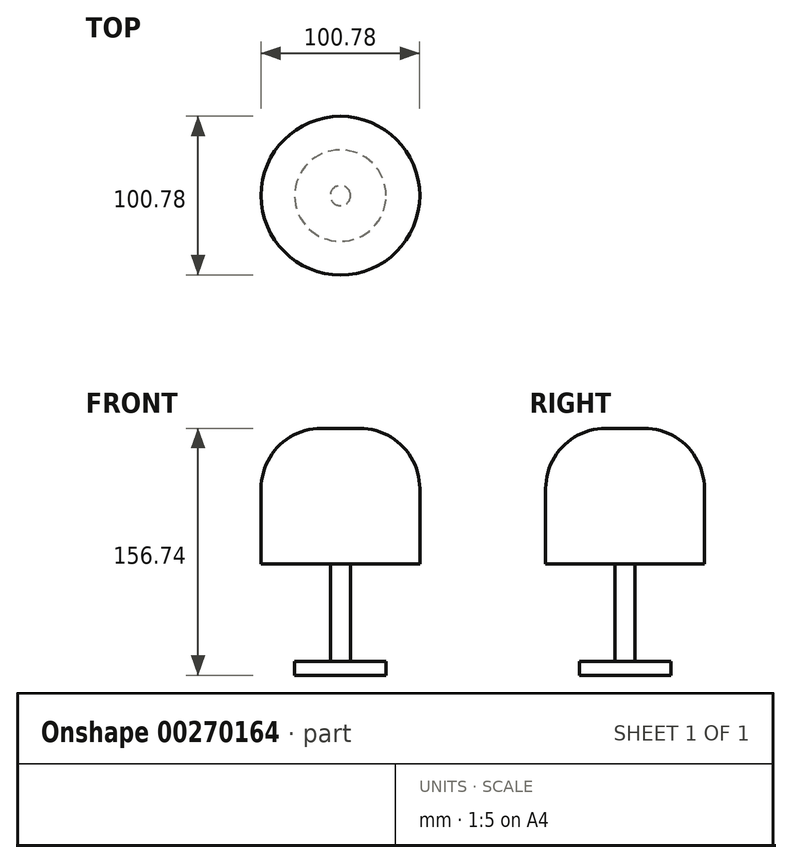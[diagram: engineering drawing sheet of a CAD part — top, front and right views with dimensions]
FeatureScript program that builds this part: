
annotation { "Feature Type Name" : "Feature", "Feature Type Description" : "" }
export const myFeature = defineFeature(function(context is Context, id is Id, definition is map)
    precondition{}
    {
        {
            var Q0;
            Q0=qCreatedBy(makeId("Front.planeOp"),FACE);
            var sketch = newSketch(context, id + "F0", { "sketchPlane" : qUnion([Q0])});
            skLineSegment(sketch, "E0", {"start": v(0, -77.09) * mm, "end": v(-29.03, -77.09) * mm});
            skLineSegment(sketch, "E1", {"start": v(-29.03, -77.09) * mm, "end": v(-29.03, -68.2) * mm});
            skLineSegment(sketch, "E2", {"start": v(-29.03, -68.2) * mm, "end": v(-6.42, -68.2) * mm});
            skLineSegment(sketch, "E3", {"start": v(-6.42, -68.2) * mm, "end": v(-6.42, -6.45) * mm});
            skLineSegment(sketch, "E4", {"start": v(-6.42, -6.45) * mm, "end": v(-50.4, -6.45) * mm});
            skLineSegment(sketch, "E5", {"start": v(-50.4, -6.45) * mm, "end": v(-50.4, 41.55) * mm});
            skLineSegment(sketch, "E6", {"start": v(-12.3, 79.65) * mm, "end": v(0, 79.65) * mm});
            skLineSegment(sketch, "E7", {"start": v(0, 79.65) * mm, "end": v(0, -77.09) * mm});
            skPoint(sketch, "E8.visualSharp", {"position": v(-50.4, 79.65) * mm});
            skArc(sketch, "E8.filletArc", {"start": v(-12.3, 79.65) * mm, "mid": v(-39.23, 68.5) * mm, "end": v(-50.4, 41.55) * mm});
            skSolve(sketch);
        }
        {
            var Q0;
            Q0 = qSketchRegion(id + "F0", true);
            var Q1;
            Q1=sQuery(id+"F0.wireOp",EDGE,"E7");
            revolve(context, id + "F1", {"entities" : qUnion([Q0]), "axis" : qUnion([Q1]), "revolveType" : RevolveType.FULL});
        }
    });
